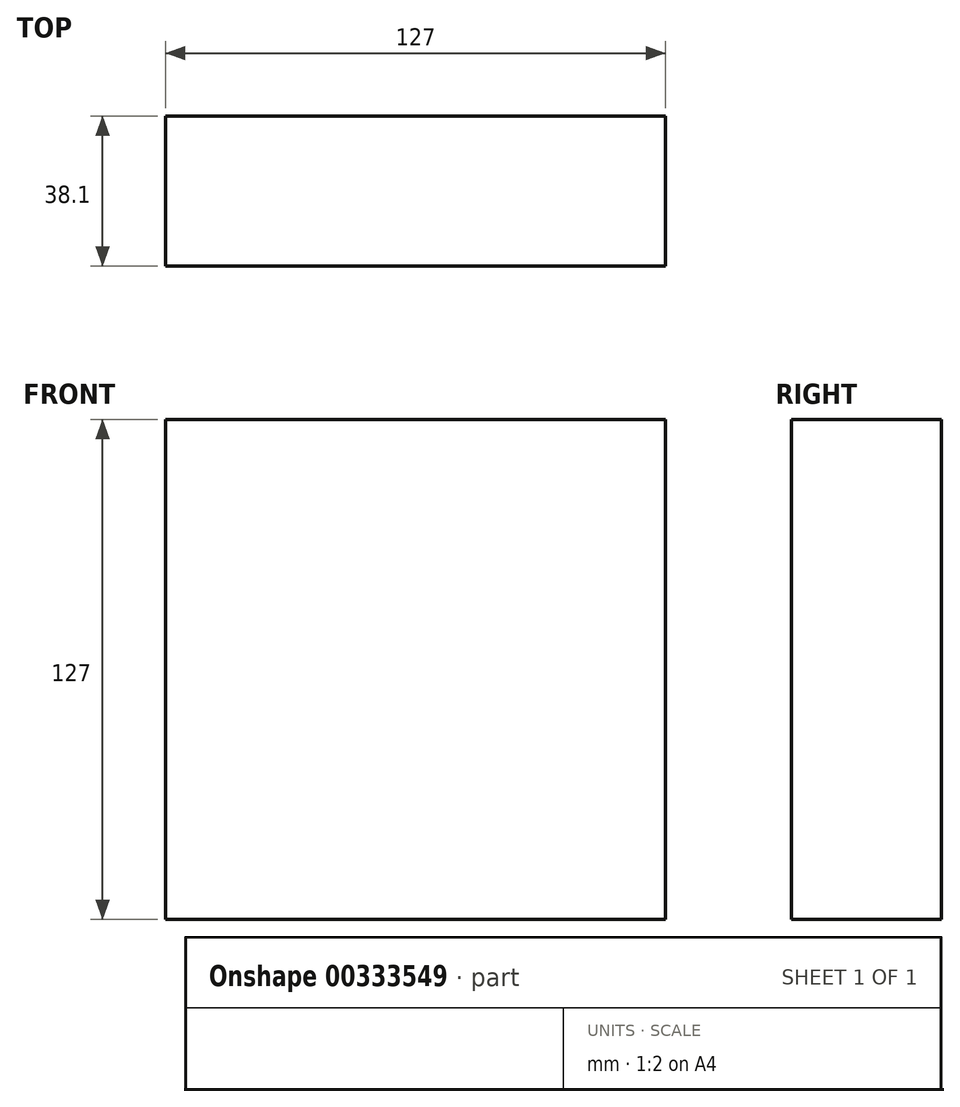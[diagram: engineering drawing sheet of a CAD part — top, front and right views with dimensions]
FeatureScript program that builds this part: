
annotation { "Feature Type Name" : "Feature", "Feature Type Description" : "" }
export const myFeature = defineFeature(function(context is Context, id is Id, definition is map)
    precondition{}
    {
        {
            var Q0;
            Q0=qCreatedBy(makeId("Top.planeOp"),FACE);
            var sketch = newSketch(context, id + "F0", { "sketchPlane" : qUnion([Q0])});
            skLineSegment(sketch, "E0", {"start": v(0, 0) * mm, "end": v(-63.5, 0) * mm});
            skLineSegment(sketch, "E1.bottom", {"start": v(-63.5, 0) * mm, "end": v(63.5, 0) * mm});
            skLineSegment(sketch, "E1.top", {"start": v(-63.5, -38.1) * mm, "end": v(63.5, -38.1) * mm});
            skLineSegment(sketch, "E1.left", {"start": v(-63.5, 0) * mm, "end": v(-63.5, -38.1) * mm});
            skLineSegment(sketch, "E1.right", {"start": v(63.5, 0) * mm, "end": v(63.5, -38.1) * mm});
            skSolve(sketch);
        }
        {
            var Q0;
            Q0 = qSketchRegion(id + "F0", true);
            extrude(context, id + "F1", {"entities" : qUnion([Q0]), "depth" : 127 * mm, "offsetDistance" : 25.4 * mm});
        }
    });
